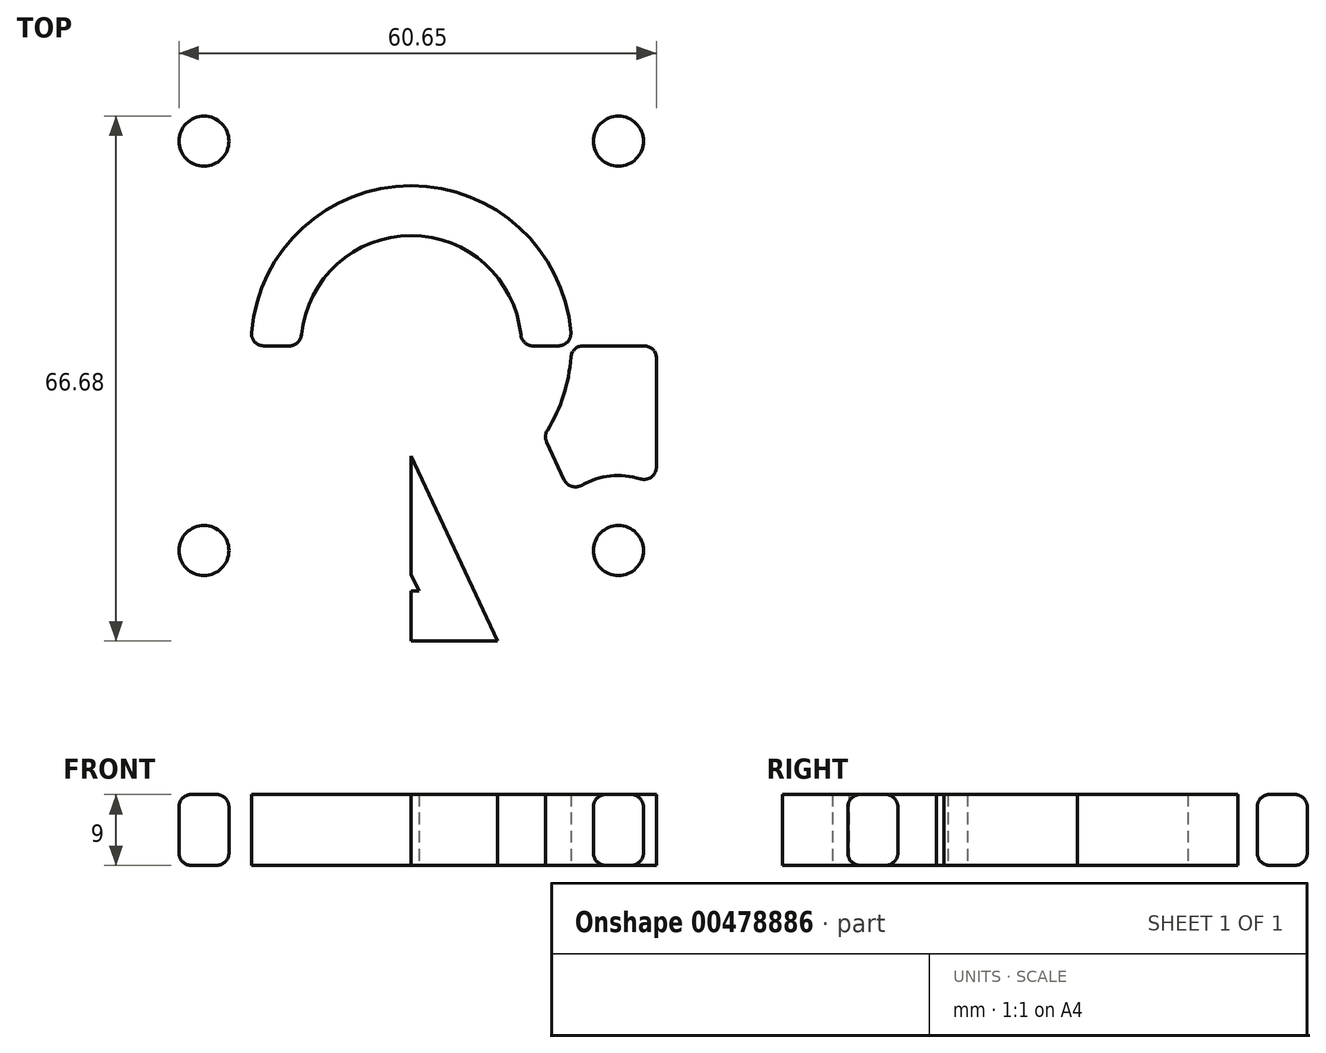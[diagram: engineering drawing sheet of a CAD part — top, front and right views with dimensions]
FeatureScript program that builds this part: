
annotation { "Feature Type Name" : "Feature", "Feature Type Description" : "" }
export const myFeature = defineFeature(function(context is Context, id is Id, definition is map)
    precondition{}
    {
        {
            var Q0;
            Q0=qCreatedBy(makeId("Top.planeOp"),FACE);
            var sketch = newSketch(context, id + "F0", { "sketchPlane" : qUnion([Q0])});
            skLineSegment(sketch, "E0", {"start": v(0, 60) * mm, "end": v(0, -60) * mm});
            skLineSegment(sketch, "E1", {"start": v(-70, 0) * mm, "end": v(70, 0) * mm});
            skLineSegment(sketch, "E2", {"start": v(-29.5, 37.5) * mm, "end": v(29.5, 37.5) * mm});
            skLineSegment(sketch, "E3", {"start": v(-29.5, -37.5) * mm, "end": v(10.96, -37.5) * mm});
            skCircle(sketch, "E4", {"center": v(-26.32, 26) * mm, "radius": 3.17 * mm});
            skCircle(sketch, "E5", {"center": v(-26.32, -26) * mm, "radius": 3.17 * mm});
            skCircle(sketch, "E6", {"center": v(26.32, -26) * mm, "radius": 3.17 * mm});
            skCircle(sketch, "E7", {"center": v(26.32, 26) * mm, "radius": 3.17 * mm});
            skArc(sketch, "E8", {"start": v(9.36, -10.41) * mm, "mid": v(-5.01, 13.07) * mm, "end": v(0, -14) * mm});
            skLineSegment(sketch, "E9", {"start": v(-37.5, -29.5) * mm, "end": v(-37.5, 29.5) * mm});
            skLineSegment(sketch, "E10", {"start": v(37.5, -29.5) * mm, "end": v(37.5, 29.5) * mm});
            skArc(sketch, "E11", {"start": v(-29.5, 37.5) * mm, "mid": v(-35.16, 35.16) * mm, "end": v(-37.5, 29.5) * mm});
            skArc(sketch, "E12", {"start": v(37.5, 29.5) * mm, "mid": v(35.16, 35.16) * mm, "end": v(29.5, 37.5) * mm});
            skArc(sketch, "E13", {"start": v(29.5, -37.5) * mm, "mid": v(35.16, -35.16) * mm, "end": v(37.5, -29.5) * mm});
            skArc(sketch, "E14", {"start": v(-37.5, -29.5) * mm, "mid": v(-35.16, -35.16) * mm, "end": v(-29.5, -37.5) * mm});
            skLineSegment(sketch, "E15", {"start": v(0, -14) * mm, "end": v(10.96, -37.5) * mm});
            skLineSegment(sketch, "E16", {"start": v(9.36, -10.41) * mm, "end": v(22, -37.5) * mm});
            skLineSegment(sketch, "E17", {"start": v(22, -37.5) * mm, "end": v(29.5, -37.5) * mm});
            skLineSegment(sketch, "E18", {"start": v(-31.15, -17.79) * mm, "end": v(-31.15, 17.79) * mm});
            skLineSegment(sketch, "E19", {"start": v(-18.31, -31.15) * mm, "end": v(1, -31.15) * mm});
            skLineSegment(sketch, "E20", {"start": v(-4.26, -19.9) * mm, "end": v(1, -31.15) * mm});
            skArc(sketch, "E21", {"start": v(16.84, -11.43) * mm, "mid": v(-7.59, 18.88) * mm, "end": v(-4.26, -19.9) * mm});
            skLineSegment(sketch, "E22", {"start": v(16.84, -11.43) * mm, "end": v(20.22, -18.68) * mm});
            skLineSegment(sketch, "E23", {"start": v(31.15, -17.79) * mm, "end": v(31.15, 17.79) * mm});
            skLineSegment(sketch, "E24", {"start": v(-18.31, 31.15) * mm, "end": v(18.31, 31.15) * mm});
            skArc(sketch, "E25", {"start": v(-31.15, 17.79) * mm, "mid": v(-19.46, 19.4) * mm, "end": v(-18.31, 31.15) * mm});
            skArc(sketch, "E26", {"start": v(-18.31, -31.15) * mm, "mid": v(-19.46, -19.4) * mm, "end": v(-31.15, -17.79) * mm});
            skArc(sketch, "E27", {"start": v(31.15, -17.79) * mm, "mid": v(25.55, -16.5) * mm, "end": v(20.22, -18.68) * mm});
            skArc(sketch, "E28", {"start": v(18.31, 31.15) * mm, "mid": v(19.46, 19.4) * mm, "end": v(31.15, 17.79) * mm});
            skSolve(sketch);
        }
        {
            var Q0;
            Q0=makeQuery(id+"F0.imprint","IMPRINT",FACE,{"disambiguationData":[TD([[makeQuery(id+"F0.imprint","IMPRINT",EDGE,{"derivedFrom":sQuery(id+"F0.wireOp",EDGE,"E4")}),1.0]])]});
            var Q1;
            Q1=makeQuery(id+"F0.imprint","IMPRINT",FACE,{"disambiguationData":[TD([[makeQuery(id+"F0.imprint","IMPRINT",EDGE,{"derivedFrom":sQuery(id+"F0.wireOp",EDGE,"E7")}),1.0]])]});
            var Q2;
            Q2=makeQuery(id+"F0.imprint","IMPRINT",FACE,{"disambiguationData":[TD([[makeQuery(id+"F0.imprint","IMPRINT",EDGE,{"derivedFrom":sQuery(id+"F0.wireOp",EDGE,"E6")}),1.0]])]});
            var Q3;
            {var subQ0=sQuery(id+"F0.wireOp",EDGE,"E21");var subQ5=sQuery(id+"F0.wireOp",EDGE,"E1");var subQ6=makeQuery(id+"F0.imprint","INTERSECT",VERTEX,{"disambiguationData":[OD(0.0)],"derivedFrom":[subQ5,subQ0]});Q3=makeQuery(id+"F0.imprint","IMPRINT",FACE,{"disambiguationData":[TD([[makeQuery(id+"F0.imprint","IMPRINT",EDGE,{"disambiguationData":[TD([[subQ6,-1.0]])],"derivedFrom":subQ5}),-1.0]])]});}
            var Q4;
            {var subQ0=sQuery(id+"F0.wireOp",EDGE,"E21");var subQ1=sQuery(id+"F0.wireOp",EDGE,"E0");var subQ2=makeQuery(id+"F0.imprint","INTERSECT",VERTEX,{"derivedFrom":[subQ1,subQ0]});Q4=makeQuery(id+"F0.imprint","IMPRINT",FACE,{"disambiguationData":[TD([[makeQuery(id+"F0.imprint","IMPRINT",EDGE,{"disambiguationData":[TD([[subQ2,-1.0]])],"derivedFrom":subQ1}),1.0]])]});}
            var Q5;
            {var subQ0=sQuery(id+"F0.wireOp",EDGE,"E21");var subQ1=sQuery(id+"F0.wireOp",EDGE,"E0");var subQ2=makeQuery(id+"F0.imprint","INTERSECT",VERTEX,{"derivedFrom":[subQ1,subQ0]});Q5=makeQuery(id+"F0.imprint","IMPRINT",FACE,{"disambiguationData":[TD([[makeQuery(id+"F0.imprint","IMPRINT",EDGE,{"disambiguationData":[TD([[subQ2,-1.0]])],"derivedFrom":subQ1}),-1.0]])]});}
            var Q6;
            Q6=makeQuery(id+"F0.imprint","IMPRINT",FACE,{"disambiguationData":[TD([[makeQuery(id+"F0.imprint","IMPRINT",EDGE,{"derivedFrom":sQuery(id+"F0.wireOp",EDGE,"E5")}),1.0]])]});
            var Q7;
            {var subQ0=sQuery(id+"F0.wireOp",EDGE,"E15");Q7=makeQuery(id+"F0.imprint","IMPRINT",FACE,{"disambiguationData":[TD([[makeQuery(id+"F0.imprint","IMPRINT",EDGE,{"derivedFrom":subQ0}),-1.0]])]});}
            extrude(context, id + "F1", {"entities" : qUnion([Q0, Q1, Q2, Q3, Q4, Q5, Q6, Q7]), "depth" : 9 * mm});
        }
        {
            var Q0;
            Q0=makeQuery(id+"F1.opExtrude","SWEPT_EDGE",EDGE,{"disambiguationData":[OSD([sQuery(id+"F0.wireOp",EDGE,"E8"),sQuery(id+"F0.wireOp",EDGE,"E16")])]});
            var Q1;
            Q1=makeQuery(id+"F1.opExtrude","SWEPT_EDGE",EDGE,{"disambiguationData":[OSD([sQuery(id+"F0.wireOp",EDGE,"E0"),sQuery(id+"F0.wireOp",EDGE,"E8"),sQuery(id+"F0.wireOp",EDGE,"E15")])]});
            var Q2;
            Q2=makeQuery(id+"F1.opExtrude","SWEPT_EDGE",EDGE,{"disambiguationData":[OSD([sQuery(id+"F0.wireOp",EDGE,"E21"),sQuery(id+"F0.wireOp",EDGE,"E22")])]});
            var Q3;
            Q3=makeQuery(id+"F1.opExtrude","SWEPT_EDGE",EDGE,{"disambiguationData":[OSD([sQuery(id+"F0.wireOp",EDGE,"E20"),sQuery(id+"F0.wireOp",EDGE,"E21")])]});
            var Q4;
            Q4=makeQuery(id+"F1.opExtrude","SWEPT_EDGE",EDGE,{"disambiguationData":[OSD([sQuery(id+"F0.wireOp",EDGE,"E16"),sQuery(id+"F0.wireOp",EDGE,"E17")])]});
            var Q5;
            Q5=makeQuery(id+"F1.opExtrude","SWEPT_EDGE",EDGE,{"disambiguationData":[OSD([sQuery(id+"F0.wireOp",EDGE,"E3"),sQuery(id+"F0.wireOp",EDGE,"E15")])]});
            var Q6;
            Q6=makeQuery(id+"F1.opExtrude","SWEPT_EDGE",EDGE,{"disambiguationData":[OSD([sQuery(id+"F0.wireOp",EDGE,"E23"),sQuery(id+"F0.wireOp",EDGE,"E28")])]});
            var Q7;
            Q7=makeQuery(id+"F1.opExtrude","SWEPT_EDGE",EDGE,{"disambiguationData":[OSD([sQuery(id+"F0.wireOp",EDGE,"E24"),sQuery(id+"F0.wireOp",EDGE,"E28")])]});
            var Q8;
            Q8=makeQuery(id+"F1.opExtrude","SWEPT_EDGE",EDGE,{"disambiguationData":[OSD([sQuery(id+"F0.wireOp",EDGE,"E24"),sQuery(id+"F0.wireOp",EDGE,"E25")])]});
            var Q9;
            Q9=makeQuery(id+"F1.opExtrude","SWEPT_EDGE",EDGE,{"disambiguationData":[OSD([sQuery(id+"F0.wireOp",EDGE,"E22"),sQuery(id+"F0.wireOp",EDGE,"E27")])]});
            var Q10;
            Q10=makeQuery(id+"F1.opExtrude","SWEPT_EDGE",EDGE,{"disambiguationData":[OSD([sQuery(id+"F0.wireOp",EDGE,"E18"),sQuery(id+"F0.wireOp",EDGE,"E26")])]});
            var Q11;
            Q11=makeQuery(id+"F1.opExtrude","SWEPT_EDGE",EDGE,{"disambiguationData":[OSD([sQuery(id+"F0.wireOp",EDGE,"E19"),sQuery(id+"F0.wireOp",EDGE,"E26")])]});
            var Q12;
            Q12=makeQuery(id+"F1.opExtrude","SWEPT_EDGE",EDGE,{"disambiguationData":[OSD([sQuery(id+"F0.wireOp",EDGE,"E23"),sQuery(id+"F0.wireOp",EDGE,"E27")])]});
            var Q13;
            Q13=makeQuery(id+"F1.opExtrude","SWEPT_EDGE",EDGE,{"disambiguationData":[OSD([sQuery(id+"F0.wireOp",EDGE,"E18"),sQuery(id+"F0.wireOp",EDGE,"E25")])]});
            var Q14;
            Q14=makeQuery(id+"F1.opExtrude","SWEPT_EDGE",EDGE,{"disambiguationData":[OSD([sQuery(id+"F0.wireOp",EDGE,"E19"),sQuery(id+"F0.wireOp",EDGE,"E20")])]});
            fillet(context, id + "F2", {"entities" : qUnion([Q0, Q1, Q2, Q3, Q4, Q5, Q6, Q7, Q8, Q9, Q10, Q11, Q12, Q13, Q14]), "radius" : 25 / 16 * mm, "tangentPropagation" : true, "allowEdgeOverflow" : false});
        }
        {
            var Q0;
            Q0=makeQuery(id+"F1.opExtrude","CAP_FACE",FACE,{"disambiguationData":[OSD([sQuery(id+"F0.wireOp",EDGE,"E2"),sQuery(id+"F0.wireOp",EDGE,"E3"),sQuery(id+"F0.wireOp",EDGE,"E4"),sQuery(id+"F0.wireOp",EDGE,"E5"),sQuery(id+"F0.wireOp",EDGE,"E6"),sQuery(id+"F0.wireOp",EDGE,"E7"),sQuery(id+"F0.wireOp",EDGE,"E8"),sQuery(id+"F0.wireOp",EDGE,"E9"),sQuery(id+"F0.wireOp",EDGE,"E10"),sQuery(id+"F0.wireOp",EDGE,"E11"),sQuery(id+"F0.wireOp",EDGE,"E12"),sQuery(id+"F0.wireOp",EDGE,"E13"),sQuery(id+"F0.wireOp",EDGE,"E14"),sQuery(id+"F0.wireOp",EDGE,"E15"),sQuery(id+"F0.wireOp",EDGE,"E16"),sQuery(id+"F0.wireOp",EDGE,"E17"),sQuery(id+"F0.wireOp",EDGE,"E18"),sQuery(id+"F0.wireOp",EDGE,"E19"),sQuery(id+"F0.wireOp",EDGE,"E20"),sQuery(id+"F0.wireOp",EDGE,"E21"),sQuery(id+"F0.wireOp",EDGE,"E22"),sQuery(id+"F0.wireOp",EDGE,"E23"),sQuery(id+"F0.wireOp",EDGE,"E24"),sQuery(id+"F0.wireOp",EDGE,"E25"),sQuery(id+"F0.wireOp",EDGE,"E26"),sQuery(id+"F0.wireOp",EDGE,"E27"),sQuery(id+"F0.wireOp",EDGE,"E28")])],"isStart":true});
            var Q1;
            Q1=makeQuery(id+"F1.opExtrude","CAP_FACE",FACE,{"disambiguationData":[OSD([sQuery(id+"F0.wireOp",EDGE,"E2"),sQuery(id+"F0.wireOp",EDGE,"E3"),sQuery(id+"F0.wireOp",EDGE,"E4"),sQuery(id+"F0.wireOp",EDGE,"E5"),sQuery(id+"F0.wireOp",EDGE,"E6"),sQuery(id+"F0.wireOp",EDGE,"E7"),sQuery(id+"F0.wireOp",EDGE,"E8"),sQuery(id+"F0.wireOp",EDGE,"E9"),sQuery(id+"F0.wireOp",EDGE,"E10"),sQuery(id+"F0.wireOp",EDGE,"E11"),sQuery(id+"F0.wireOp",EDGE,"E12"),sQuery(id+"F0.wireOp",EDGE,"E13"),sQuery(id+"F0.wireOp",EDGE,"E14"),sQuery(id+"F0.wireOp",EDGE,"E15"),sQuery(id+"F0.wireOp",EDGE,"E16"),sQuery(id+"F0.wireOp",EDGE,"E17"),sQuery(id+"F0.wireOp",EDGE,"E18"),sQuery(id+"F0.wireOp",EDGE,"E19"),sQuery(id+"F0.wireOp",EDGE,"E20"),sQuery(id+"F0.wireOp",EDGE,"E21"),sQuery(id+"F0.wireOp",EDGE,"E22"),sQuery(id+"F0.wireOp",EDGE,"E23"),sQuery(id+"F0.wireOp",EDGE,"E24"),sQuery(id+"F0.wireOp",EDGE,"E25"),sQuery(id+"F0.wireOp",EDGE,"E26"),sQuery(id+"F0.wireOp",EDGE,"E27"),sQuery(id+"F0.wireOp",EDGE,"E28")])],"isStart":false});
            fillet(context, id + "F3", {"entities" : qUnion([Q0, Q1]), "radius" : (25 / 16) * mm, "tangentPropagation" : true, "allowEdgeOverflow" : false});
        }
    });
